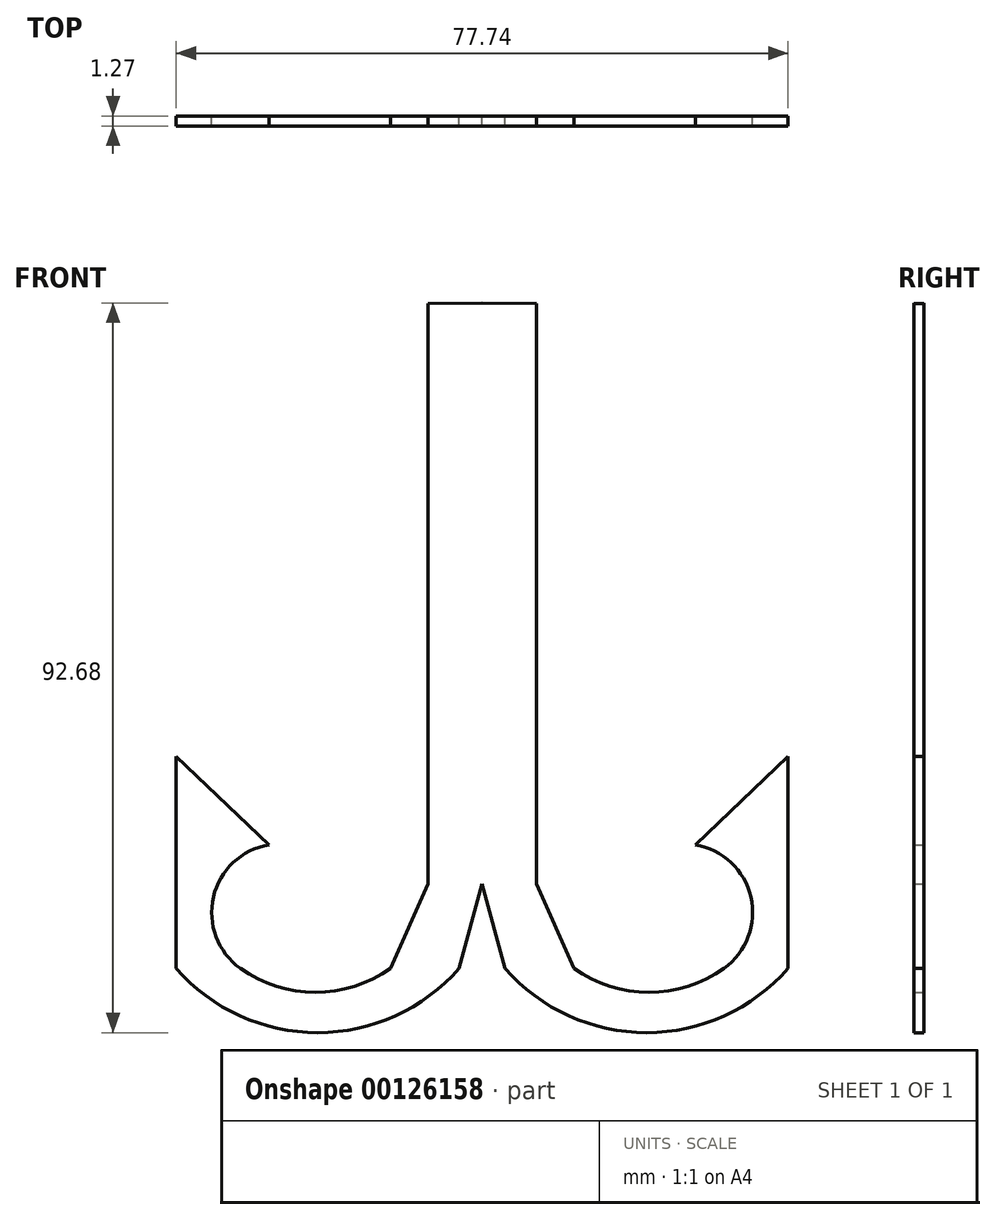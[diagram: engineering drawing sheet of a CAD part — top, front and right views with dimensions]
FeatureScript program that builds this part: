
annotation { "Feature Type Name" : "Feature", "Feature Type Description" : "" }
export const myFeature = defineFeature(function(context is Context, id is Id, definition is map)
    precondition{}
    {
        {
            var Q0;
            Q0=qCreatedBy(makeId("Front.planeOp"),FACE);
            var sketch = newSketch(context, id + "F0", { "sketchPlane" : qUnion([Q0])});
            skLineSegment(sketch, "E0", {"start": v(0, 0) * mm, "end": v(0, 73.79) * mm});
            skLineSegment(sketch, "E1", {"start": v(0, 0) * mm, "end": v(-2.91, -10.72) * mm});
            skArc(sketch, "E2", {"start": v(-38.87, -10.72) * mm, "mid": v(-20.9, -18.89) * mm, "end": v(-2.91, -10.72) * mm});
            skLineSegment(sketch, "E3", {"start": v(-38.87, -10.72) * mm, "end": v(-38.87, 16.18) * mm});
            skLineSegment(sketch, "E4", {"start": v(-38.87, 16.18) * mm, "end": v(-27.09, 4.98) * mm});
            skArc(sketch, "E5", {"start": v(-27.09, 4.98) * mm, "mid": v(-34.13, -1.66) * mm, "end": v(-30.71, -10.72) * mm});
            skArc(sketch, "E6", {"start": v(-30.71, -10.72) * mm, "mid": v(-21.18, -13.79) * mm, "end": v(-11.65, -10.72) * mm});
            skLineSegment(sketch, "E7", {"start": v(-11.65, -10.72) * mm, "end": v(-6.9, 0) * mm});
            skLineSegment(sketch, "E8", {"start": v(-6.9, 0) * mm, "end": v(-6.9, 73.75) * mm});
            skLineSegment(sketch, "E9", {"start": v(0, 73.79) * mm, "end": v(-6.9, 73.75) * mm});
            skArc(sketch, "E10.MirrorCS", {"start": v(30.71, -10.72) * mm, "mid": v(21.18, -13.79) * mm, "end": v(11.65, -10.72) * mm});
            skArc(sketch, "E11.MirrorCS", {"start": v(38.87, -10.72) * mm, "mid": v(20.9, -18.89) * mm, "end": v(2.91, -10.72) * mm});
            skLineSegment(sketch, "E12.MirrorCS", {"start": v(0, 0) * mm, "end": v(2.91, -10.72) * mm});
            skLineSegment(sketch, "E13.MirrorCS", {"start": v(11.65, -10.72) * mm, "end": v(6.9, 0) * mm});
            skLineSegment(sketch, "E14.MirrorCS", {"start": v(6.9, 0) * mm, "end": v(6.9, 73.75) * mm});
            skLineSegment(sketch, "E15.MirrorCS", {"start": v(38.87, -10.72) * mm, "end": v(38.87, 16.18) * mm});
            skLineSegment(sketch, "E16.MirrorCS", {"start": v(38.87, 16.18) * mm, "end": v(27.09, 4.98) * mm});
            skArc(sketch, "E17.MirrorCS", {"start": v(27.09, 4.98) * mm, "mid": v(34.13, -1.66) * mm, "end": v(30.71, -10.72) * mm});
            skLineSegment(sketch, "E18.MirrorCS", {"start": v(0, 73.79) * mm, "end": v(6.9, 73.75) * mm});
            skSolve(sketch);
        }
        {
            var Q0;
            Q0 = qSketchRegion(id + "F0", true);
            extrude(context, id + "F1", {"entities" : qUnion([Q0]), "depth" : 1.27 * mm});
        }
    });
